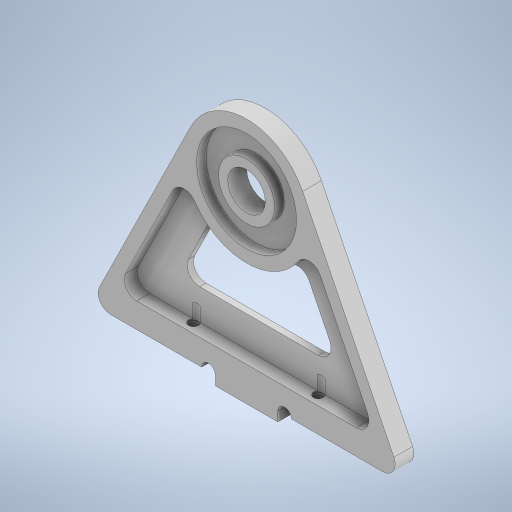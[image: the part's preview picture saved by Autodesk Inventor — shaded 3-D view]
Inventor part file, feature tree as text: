
AUTODESK INVENTOR PART (.ipt)
format: ipt  version: 2024 (Build 280153000, 153)  size: 364,032 bytes
history: native  units: mm
features: extrude x4, sketch x4, fillet x3, other x1, hole x1, projected_geometry x1
ambient origin geometry x8: Origin, YZ Plane, XZ Plane, XY Plane, X Axis, Y Axis, Z Axis, Center Point
bodies: Body1 (feature_tree)
feature tree (14):
  other  "ソリッド1"
  extrude  "押し出し1"  Depth=6.0mm
  fillet  "フィレット1"  Radius=20.0mm
  hole  "穴1"  [1 undecoded]
  sketch  "スケッチ3"
  extrude  "押し出し2"  Depth=1.5mm
  fillet  "フィレット2"  Radius=10.0mm
  extrude  "押し出し3"  Depth=2.2mm
  extrude  "押し出し4"  Depth=2.2mm
  fillet  "フィレット3"  Radius=50.0mm
  sketch  "スケッチ1"
  sketch  "スケッチ2"
  projected_geometry  "投影ループ1"
  sketch  "スケッチ4"
note: 1 required parameter value undecoded (feature->parameter linkage not recoverable at this tier; creation-order binding heuristic only, values carry confidence <= 0.55)
